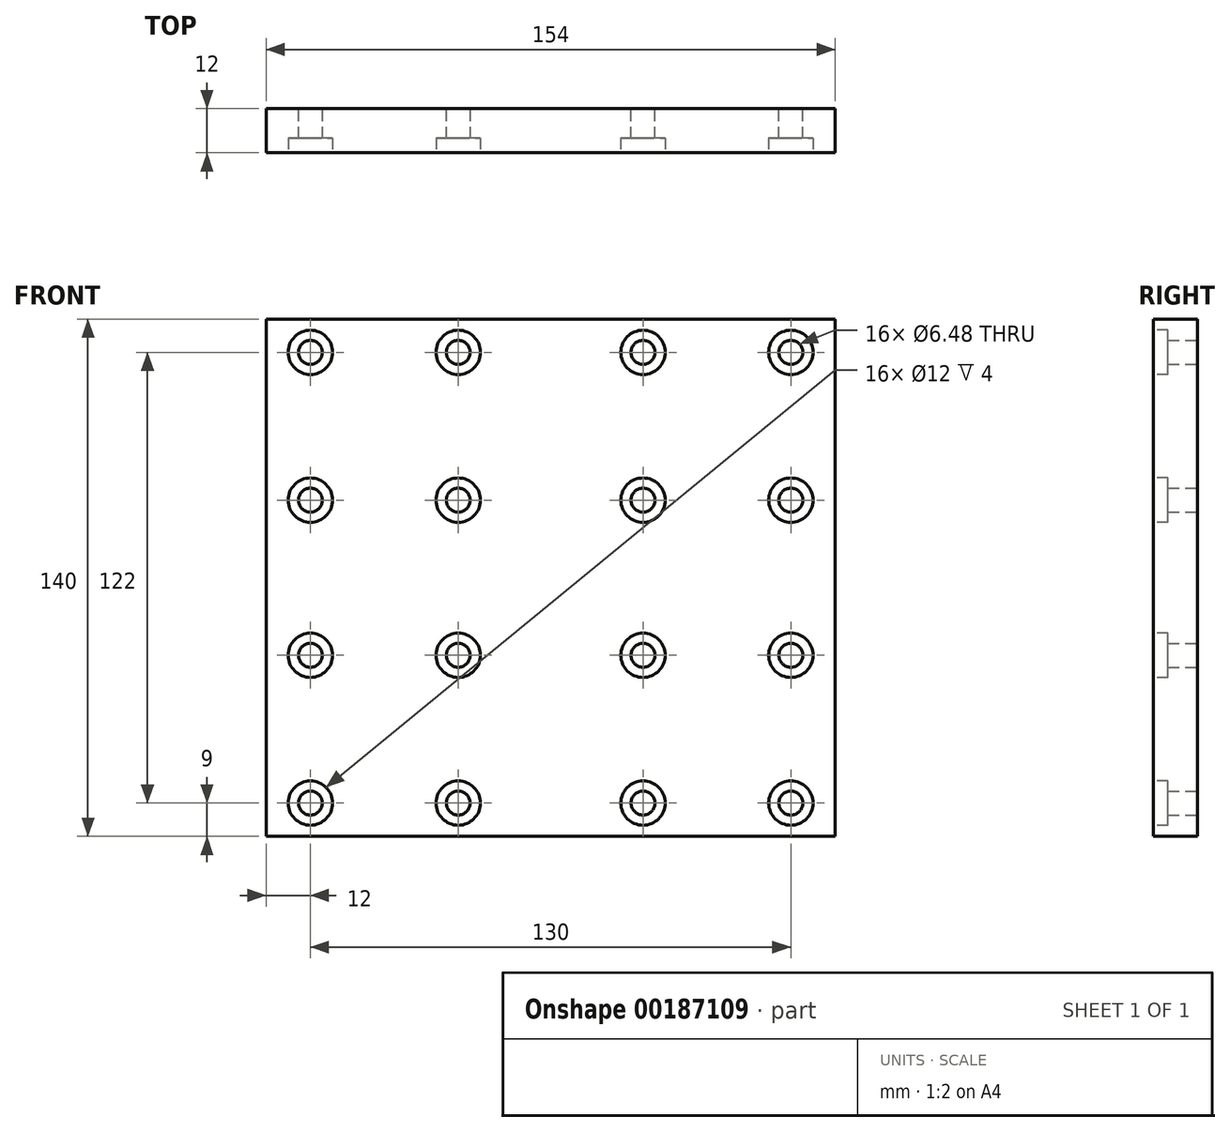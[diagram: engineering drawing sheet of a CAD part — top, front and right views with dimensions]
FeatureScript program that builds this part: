
annotation { "Feature Type Name" : "Feature", "Feature Type Description" : "" }
export const myFeature = defineFeature(function(context is Context, id is Id, definition is map)
    precondition{}
    {
        {
            var Q0;
            Q0=qCreatedBy(makeId("Front.planeOp"),FACE);
            var sketch = newSketch(context, id + "F0", { "sketchPlane" : qUnion([Q0])});
            skLineSegment(sketch, "E0.bottom", {"start": v(77, -70) * mm, "end": v(-77, -70) * mm});
            skLineSegment(sketch, "E0.top", {"start": v(77, 70) * mm, "end": v(-77, 70) * mm});
            skLineSegment(sketch, "E0.left", {"start": v(77, -70) * mm, "end": v(77, 70) * mm});
            skLineSegment(sketch, "E0.right", {"start": v(-77, -70) * mm, "end": v(-77, 70) * mm});
            skPoint(sketch, "E0.middle", {"position": v(0, 0) * mm});
            skLineSegment(sketch, "E1", {"start": v(-65, 70) * mm, "end": v(-65, -70) * mm, "construction": true});
            skLineSegment(sketch, "E2", {"start": v(65, 70) * mm, "end": v(65, -70) * mm, "construction": true});
            skLineSegment(sketch, "E3", {"start": v(-77, 61) * mm, "end": v(77, 61) * mm, "construction": true});
            skLineSegment(sketch, "E4", {"start": v(-77, 21) * mm, "end": v(77, 21) * mm, "construction": true});
            skLineSegment(sketch, "E5", {"start": v(-25, 70) * mm, "end": v(-25, -70) * mm, "construction": true});
            skLineSegment(sketch, "E6", {"start": v(25, 70) * mm, "end": v(25, -70) * mm, "construction": true});
            skLineSegment(sketch, "E7", {"start": v(-77, -61) * mm, "end": v(77, -61) * mm, "construction": true});
            skLineSegment(sketch, "E8", {"start": v(-77, -21) * mm, "end": v(77, -21) * mm, "construction": true});
            skCircle(sketch, "E9", {"center": v(-65, 61) * mm, "radius": 3.24 * mm});
            skCircle(sketch, "E10", {"center": v(-25, 61) * mm, "radius": 3.24 * mm});
            skCircle(sketch, "E11", {"center": v(25, 61) * mm, "radius": 3.24 * mm});
            skCircle(sketch, "E12", {"center": v(65, 61) * mm, "radius": 3.24 * mm});
            skCircle(sketch, "E13", {"center": v(-65, 21) * mm, "radius": 3.24 * mm});
            skCircle(sketch, "E14", {"center": v(-25, 21) * mm, "radius": 3.24 * mm});
            skCircle(sketch, "E15", {"center": v(25, 21) * mm, "radius": 3.24 * mm});
            skCircle(sketch, "E16", {"center": v(65, 21) * mm, "radius": 3.24 * mm});
            skCircle(sketch, "E17", {"center": v(-65, -21) * mm, "radius": 3.24 * mm});
            skCircle(sketch, "E18", {"center": v(-25, -21) * mm, "radius": 3.24 * mm});
            skCircle(sketch, "E19", {"center": v(25, -21) * mm, "radius": 3.24 * mm});
            skCircle(sketch, "E20", {"center": v(65, -21) * mm, "radius": 3.24 * mm});
            skCircle(sketch, "E21", {"center": v(-65, -61) * mm, "radius": 3.24 * mm});
            skCircle(sketch, "E22", {"center": v(-25, -61) * mm, "radius": 3.24 * mm});
            skCircle(sketch, "E23", {"center": v(25, -61) * mm, "radius": 3.24 * mm});
            skCircle(sketch, "E24", {"center": v(65, -61) * mm, "radius": 3.24 * mm});
            skSolve(sketch);
        }
        {
            var Q0;
            Q0=makeQuery(id+"F0.imprint","IMPRINT",FACE,{"disambiguationData":[TD([[makeQuery(id+"F0.imprint","IMPRINT",EDGE,{"derivedFrom":sQuery(id+"F0.wireOp",EDGE,"E0.bottom")}),-1.0]])]});
            extrude(context, id + "F1", {"entities" : qUnion([Q0]), "depth" : 12 * mm});
        }
        {
            var Q0;
            Q0=makeQuery(id+"F1.opExtrude","CAP_FACE",FACE,{"disambiguationData":[OSD([sQuery(id+"F0.wireOp",EDGE,"E0.bottom"),sQuery(id+"F0.wireOp",EDGE,"E0.top"),sQuery(id+"F0.wireOp",EDGE,"E0.left"),sQuery(id+"F0.wireOp",EDGE,"E0.right"),sQuery(id+"F0.wireOp",EDGE,"E9"),sQuery(id+"F0.wireOp",EDGE,"E10"),sQuery(id+"F0.wireOp",EDGE,"E11"),sQuery(id+"F0.wireOp",EDGE,"E12"),sQuery(id+"F0.wireOp",EDGE,"E13"),sQuery(id+"F0.wireOp",EDGE,"E14"),sQuery(id+"F0.wireOp",EDGE,"E15"),sQuery(id+"F0.wireOp",EDGE,"E16"),sQuery(id+"F0.wireOp",EDGE,"E17"),sQuery(id+"F0.wireOp",EDGE,"E18"),sQuery(id+"F0.wireOp",EDGE,"E19"),sQuery(id+"F0.wireOp",EDGE,"E20"),sQuery(id+"F0.wireOp",EDGE,"E21"),sQuery(id+"F0.wireOp",EDGE,"E22"),sQuery(id+"F0.wireOp",EDGE,"E23"),sQuery(id+"F0.wireOp",EDGE,"E24")])],"isStart":false});
            var sketch = newSketch(context, id + "F2", { "sketchPlane" : qUnion([Q0])});
            skCircle(sketch, "E25", {"center": v(-65, 61) * mm, "radius": 6 * mm});
            skCircle(sketch, "E26", {"center": v(-25, 61) * mm, "radius": 6 * mm});
            skCircle(sketch, "E27", {"center": v(25, 61) * mm, "radius": 6 * mm});
            skCircle(sketch, "E28", {"center": v(65, 61) * mm, "radius": 6 * mm});
            skCircle(sketch, "E29", {"center": v(-65, 21) * mm, "radius": 6 * mm});
            skCircle(sketch, "E30", {"center": v(-25, 21) * mm, "radius": 6 * mm});
            skCircle(sketch, "E31", {"center": v(25, 21) * mm, "radius": 6 * mm});
            skCircle(sketch, "E32", {"center": v(65, 21) * mm, "radius": 6 * mm});
            skCircle(sketch, "E33", {"center": v(65, -21) * mm, "radius": 6 * mm});
            skCircle(sketch, "E34", {"center": v(25, -21) * mm, "radius": 6 * mm});
            skCircle(sketch, "E35", {"center": v(-25, -21) * mm, "radius": 6 * mm});
            skCircle(sketch, "E36", {"center": v(-65, -21) * mm, "radius": 6 * mm});
            skCircle(sketch, "E37", {"center": v(-65, -61) * mm, "radius": 6 * mm});
            skCircle(sketch, "E38", {"center": v(-25, -61) * mm, "radius": 6 * mm});
            skCircle(sketch, "E39", {"center": v(25, -61) * mm, "radius": 6 * mm});
            skCircle(sketch, "E40", {"center": v(65, -61) * mm, "radius": 6 * mm});
            skSolve(sketch);
        }
        {
            var Q0;
            Q0=makeQuery(id+"F2.imprint","IMPRINT",FACE,{"disambiguationData":[TD([[makeQuery(id+"F2.imprint","IMPRINT",EDGE,{"derivedFrom":sQuery(id+"F2.wireOp",EDGE,"E25")}),1.0]])]});
            var Q1;
            Q1=makeQuery(id+"F2.imprint","IMPRINT",FACE,{"disambiguationData":[TD([[makeQuery(id+"F2.imprint","IMPRINT",EDGE,{"derivedFrom":sQuery(id+"F2.wireOp",EDGE,"E26")}),1.0]])]});
            var Q2;
            Q2=makeQuery(id+"F2.imprint","IMPRINT",FACE,{"disambiguationData":[TD([[makeQuery(id+"F2.imprint","IMPRINT",EDGE,{"derivedFrom":sQuery(id+"F2.wireOp",EDGE,"E27")}),1.0]])]});
            var Q3;
            Q3=makeQuery(id+"F2.imprint","IMPRINT",FACE,{"disambiguationData":[TD([[makeQuery(id+"F2.imprint","IMPRINT",EDGE,{"derivedFrom":sQuery(id+"F2.wireOp",EDGE,"E28")}),1.0]])]});
            var Q4;
            Q4=makeQuery(id+"F2.imprint","IMPRINT",FACE,{"disambiguationData":[TD([[makeQuery(id+"F2.imprint","IMPRINT",EDGE,{"derivedFrom":sQuery(id+"F2.wireOp",EDGE,"E32")}),1.0]])]});
            var Q5;
            Q5=makeQuery(id+"F2.imprint","IMPRINT",FACE,{"disambiguationData":[TD([[makeQuery(id+"F2.imprint","IMPRINT",EDGE,{"derivedFrom":sQuery(id+"F2.wireOp",EDGE,"E31")}),1.0]])]});
            var Q6;
            Q6=makeQuery(id+"F2.imprint","IMPRINT",FACE,{"disambiguationData":[TD([[makeQuery(id+"F2.imprint","IMPRINT",EDGE,{"derivedFrom":sQuery(id+"F2.wireOp",EDGE,"E30")}),1.0]])]});
            var Q7;
            Q7=makeQuery(id+"F2.imprint","IMPRINT",FACE,{"disambiguationData":[TD([[makeQuery(id+"F2.imprint","IMPRINT",EDGE,{"derivedFrom":sQuery(id+"F2.wireOp",EDGE,"E29")}),1.0]])]});
            var Q8;
            Q8=makeQuery(id+"F2.imprint","IMPRINT",FACE,{"disambiguationData":[TD([[makeQuery(id+"F2.imprint","IMPRINT",EDGE,{"derivedFrom":sQuery(id+"F2.wireOp",EDGE,"E36")}),1.0]])]});
            var Q9;
            Q9=makeQuery(id+"F2.imprint","IMPRINT",FACE,{"disambiguationData":[TD([[makeQuery(id+"F2.imprint","IMPRINT",EDGE,{"derivedFrom":sQuery(id+"F2.wireOp",EDGE,"E35")}),1.0]])]});
            var Q10;
            Q10=makeQuery(id+"F2.imprint","IMPRINT",FACE,{"disambiguationData":[TD([[makeQuery(id+"F2.imprint","IMPRINT",EDGE,{"derivedFrom":sQuery(id+"F2.wireOp",EDGE,"E34")}),1.0]])]});
            var Q11;
            Q11=makeQuery(id+"F2.imprint","IMPRINT",FACE,{"disambiguationData":[TD([[makeQuery(id+"F2.imprint","IMPRINT",EDGE,{"derivedFrom":sQuery(id+"F2.wireOp",EDGE,"E33")}),1.0]])]});
            var Q12;
            Q12=makeQuery(id+"F2.imprint","IMPRINT",FACE,{"disambiguationData":[TD([[makeQuery(id+"F2.imprint","IMPRINT",EDGE,{"derivedFrom":sQuery(id+"F2.wireOp",EDGE,"E40")}),1.0]])]});
            var Q13;
            Q13=makeQuery(id+"F2.imprint","IMPRINT",FACE,{"disambiguationData":[TD([[makeQuery(id+"F2.imprint","IMPRINT",EDGE,{"derivedFrom":sQuery(id+"F2.wireOp",EDGE,"E39")}),1.0]])]});
            var Q14;
            Q14=makeQuery(id+"F2.imprint","IMPRINT",FACE,{"disambiguationData":[TD([[makeQuery(id+"F2.imprint","IMPRINT",EDGE,{"derivedFrom":sQuery(id+"F2.wireOp",EDGE,"E38")}),1.0]])]});
            var Q15;
            Q15=makeQuery(id+"F2.imprint","IMPRINT",FACE,{"disambiguationData":[TD([[makeQuery(id+"F2.imprint","IMPRINT",EDGE,{"derivedFrom":sQuery(id+"F2.wireOp",EDGE,"E37")}),1.0]])]});
            extrude(context, id + "F3", {"entities" : qUnion([Q0, Q1, Q2, Q3, Q4, Q5, Q6, Q7, Q8, Q9, Q10, Q11, Q12, Q13, Q14, Q15]), "operationType" : NewBodyOperationType.REMOVE, "oppositeDirection" : true, "depth" : 4 * mm});
        }
    });
